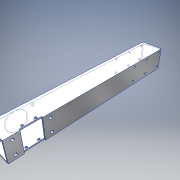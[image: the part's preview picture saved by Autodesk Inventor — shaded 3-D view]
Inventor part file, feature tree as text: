
AUTODESK INVENTOR PART (.ipt)
format: ipt  version: 2019 (Build 230136000, 136)  size: 195,072 bytes
history: native  units: in
note: dims shown in document units (in); Inventor stores cm internally (conversion verified against a paired STEP export)
features: extrude x7, sketch x7, projected_geometry x2
ambient origin geometry x8: Origin, YZ Plane, XZ Plane, XY Plane, X Axis, Y Axis, Z Axis, Center Point
bodies: Solid1 (feature_tree)
feature tree (16):
  extrude  "Extrusion1"  Depth=0.125in
  extrude  "Extrusion2"  Depth=16.0in
  extrude  "Extrusion9"  Depth=3.5in
  sketch  "Sketch11"  dims[d7=0.7in d8=18.0in d9=0.0in]
  extrude  "Extrusion11"  Depth=18.0in TaperAngle=0.0deg
  extrude  "Extrusion12"  Depth=1.654in
  extrude  "Extrusion13"  Depth=0.125in TaperAngle=0.0deg
  extrude  "Extrusion14"  Depth=1.75in
  sketch  "Sketch1"  dims[d0=2.0in d1=0.125in]
  sketch  "Sketch2"  dims[d2=16.0in d3=0.0in d4=0.21in]
  sketch  "Sketch10"  dims[d5=0.3in d6=3.5in]
  projected_geometry  "Projected Loop2"
  sketch  "Sketch12"  dims[d47=2.0in d48=1.654in]
  projected_geometry  "Projected Loop3"
  sketch  "Sketch14"  dims[d49=2.0in d50=0.125in d51=0.0in]
  sketch  "Sketch15"  dims[d54=2.0in d55=1.75in d56=0.125in d57=0.0in d67=0.25in d68=1.25in d69=1.0in d70=0.0in d71=1.0in d72=0.0in d73=0.19in d74=1.0in d75=0.0in]
